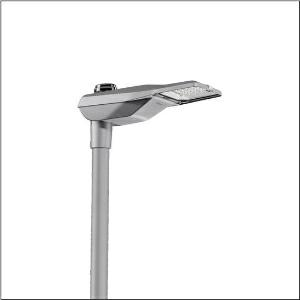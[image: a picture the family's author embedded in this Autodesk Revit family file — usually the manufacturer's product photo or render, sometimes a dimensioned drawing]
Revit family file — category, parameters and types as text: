
# Revit family: streetlight_sl_21_micro___st1_0a_5xe5d47n08db_8e26
name_source: partatom
category: Lighting Fixtures
units: mm (PartAtom-declared; Revit-internal decimal feet)

## family parameters
Cut with Voids When Loaded = No
Host = Face
Light Source = No
Part Type = Normal
Room Calculation Point = No
Round Connector Dimension = Use Diameter
Shared = No

## types (1)
- --- (1 x LED, 5320 lm, 39.1 W, 4000K)
    Apparent Load = 39 VA
    CIE Flux Codes = 37 72 97 100 100
    Color Rendering = 70
    Color Temperature = 4000K
    Default Elevation = 1800 mm
    Description = Streetlight SL 21 micro, mast luminaire, primary light control with lens, of PMMA, primary optical cover: cover, of toughened safety glass, transparent, light distribution: ST1.0a, light emission: direct distribution, primary light characteristic: asymmetric, installation type: post-top, LED, 3G 1.5mm², High Power LED, rated luminous flux: 5.320lm, luminous efficacy: 136lm/W, light colour: 740, colour temperature: 4000K, control: overheat protection, presetting dimming linear, constant luminous flux control, time-dependent luminous flux control, flexible luminous flux parameterisation, mains connection: 230..240V, AC, 50/60Hz, connection cable pre-assembled, cable length: 6,5m, wiring characteristics: H07RN-F, start of lifetime: 39W, end of service life: 41W, reduction: 18W, luminaire housing, of diecast aluminium (EN AC-44300), powder-coated, Siteco® metallic grey (DB 702S), corrosivity category C5 mid according to DIN EN ISO 12944, multi-level sealing system, sealing non-destructively replaceable, inclination adjustable: 0°, 5°, 10°, 15°, length: 528mm, width: 235mm, height: 110mm, spigot size: 76/60mm (post-top), protection rating (complete): IP66, insulation class (complete): insulation class I (protective earthing), certification: CE, ENEC, ENEC+, VDE, impact resistance: IK09, permissible operating ambient temperature for outdoor applications: -40..+50°C, standard-compliant lighting for roads and squares, packaging unit: 1 piece

Light Distribution: ST1.0a
    Height = 110 mm
    Lamp = 1 x LED
    Lamp Light Flux = 5320 lm
    Lamp Power = 39.1 W
    Lamp count = 1
    Length = 528 mm
    Luminous efficacy = 136 lm/W
    Manufacturer = Siteco
    ModVariant = No
    Model = 5XE5D47N08DB
    Number of Poles = 1
    OnlyDefault = Yes
    Power Factor = 1
    Product Name = Streetlight SL 21 micro | ST1.0a
    Product group = mast luminaire | pylon top
    ProductGroupID = 6100
    Protection Class = Protection class I
    Protection Degree = IP 66
    RLX_Detail_Level = 1
    RLX_Emergency_Light_Flux = 0 lm
    RLX_Emergency_Type = 0
    RLX_Emergency_Type_DB = No
    RlxData = <blob elided: 99921 chars, md5=02229e5b>
    Socket = socket
    Standby Power = 0 W
    System Light Flux = 5320 lm
    System Power = 39 W
    Type Comments = factory setting: luminous flux: 100 % | dim-lin: 254 | 765 mA
    Type Image = l_1294375.jpg
    URL = http://relux.com
    VarID = @adj_085853
    Voltage = 0 V
    Weight = 0.00 kg
    Width = 235 mm

## geometry (parser evidence)
native form markers: Blend x4, Sweep x10
no freeform markers — native parametric forms only
